# Revit family: Mailboxes_4C-Salsbury_Industries-Surface_Mounted-8_Door_High_Units
name_source: partatom
category: Specialty Equipment
revit_build: Autodesk Revit 2016 (Build: 20150714_1515(x64)
units: mm (PartAtom-declared; Revit-internal decimal feet)

## family parameters
Always vertical = Yes
Cut with Voids When Loaded = No
OmniClass Number = 23.40.90.14.11
OmniClass Title = Mail Boxes
Part Type = Normal
Room Calculation Point = No
Round Connector Dimension = Use Diameter
Shared = No
Work Plane-Based = No

## types (11) — shared parameters
4C Unit Height = 30.5 "
Assembly Code = C1030910
Assembly Description = Mailboxes
Depth = 17.5 "
Height = 31.594 "
Lock Material = Stainless Steel - Salsbury Finish -  Polished
Manufacturer = Salsbury Industries
MasterFormat Number = 10 55 00
MasterFormat Title = Postal Specialties
OmniClass 23 Number = 23.40.90.14.11
OmniClass 23 Title = Mail Boxes
Type Comments = Surface Mounted 4C Horizontal Mailboxes - Front Loading
URL = www.mailboxes.com
Version = 1.0 (06/30/17)

## per-type parameters (varying)
| type | 4C Unit | 4C Unit Elevation | Above Finished Floor (Bottom of Unit) | Description | Width |
| 3808S-06 | Mailboxes_4C-Salsbury_Industries-Front_Load-8_Door_High_Units : 3708S-06 FL | 26.683 " | 26.12 " | 8 Door High Unit:  6 MB1, OM2 | 17.496 " |
| 3808D-14 | Mailboxes_4C-Salsbury_Industries-Front_Load-8_Door_High_Units : 3708D-14 FL | 26.683 " | 26.12 " | 8 Door High Unit:  14 MB1, OM2 | 32.25 " |
| 3808D-13 | Mailboxes_4C-Salsbury_Industries-Front_Load-8_Door_High_Units : 3708D-13 FL | 26.683 " | 26.12 " | 8 Door High Unit:  13 MB1, OM3 | 32.25 " |
| 3808D-09 | Mailboxes_4C-Salsbury_Industries-Front_Load-8_Door_High_Units : 3708D-09 FL | 26.683 " | 26.12 " | 8 Door High Unit:  9 MB1, 1 PL5, OM2 | 32.25 " |
| 3808D-07 | Mailboxes_4C-Salsbury_Industries-Front_Load-8_Door_High_Units : 3708D-07 FL | 26.683 " | 26.12 " | 8 Door High Unit:  7 MB2, OM2 | 32.25 " |
| 3808D-04 | Mailboxes_4C-Salsbury_Industries-Front_Load-8_Door_High_Units : 3708D-04 FL | 26.683 " | 26.12 " | 8 Door High Unit:  4 MB2, 1 PL6, OM2 | 32.25 " |
| 3808S-03 | Mailboxes_4C-Salsbury_Industries-Front_Load-8_Door_High_Units : 3708S-03 FL | 26.683 " | 26.12 " | 8 Door High Unit:  3 MB2, OM2 | 17.496 " |
| 3808S-01 | Mailboxes_4C-Salsbury_Industries-Front_Load-8_Door_High_Units : 3708S-01 FL | 13.683 " | 13.12 " | 8 Door High Unit:  1 MB1, 1 PL5, OM2 | 17.496 " |
| 3808S-2P | Mailboxes_4C-Salsbury_Industries-Front_Load-8_Door_High_Units : 3708S-2P FL | 13.683 " | 13.12 " | 8 Door High Unit:  2 PL4 | 17.496 " |
| 3808S-1B | Mailboxes_4C-Salsbury_Industries-Front_Load-8_Door_High_Units : 3708S-1B FL | 13.683 " | 13.12 " | 8 Door High Unit:  1 Receptacle Bin | 17.496 " |
| 3808S-1C | Mailboxes_4C-Salsbury_Industries-Front_Load-8_Door_High_Units : 3708S-1C FL | 13.683 " | 13.12 " | 8 Door High Unit:  1 Collection Box | 17.496 " |

note: column(s) folded — value = type name in every type: Model

## geometry (parser evidence)
native form markers: Blend x6, Extrusion x1, Sweep x17
no freeform markers — native parametric forms only
